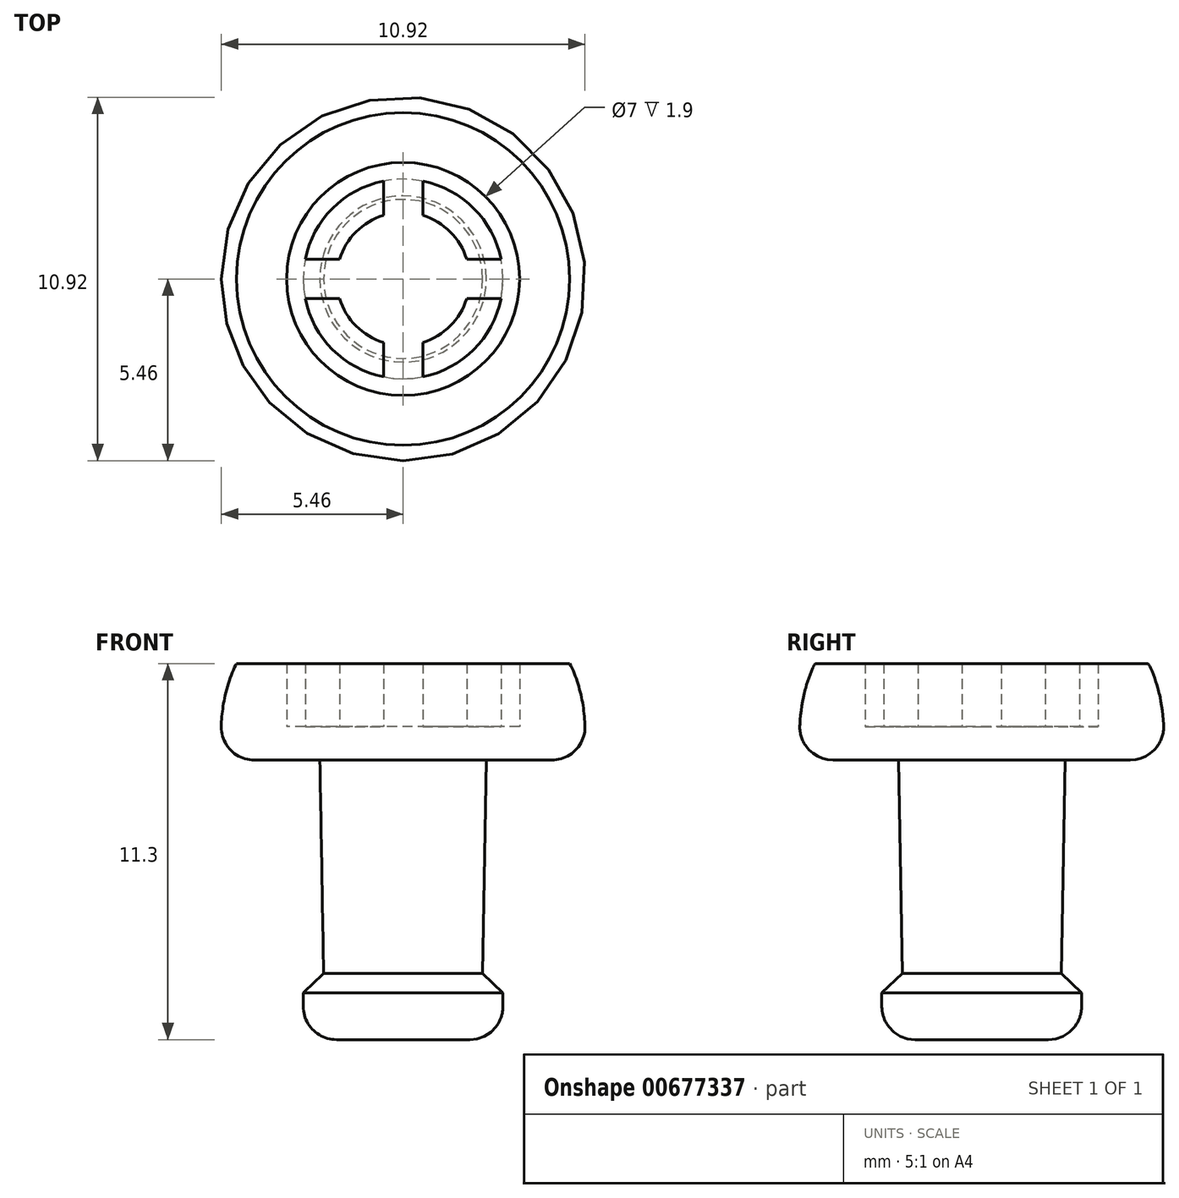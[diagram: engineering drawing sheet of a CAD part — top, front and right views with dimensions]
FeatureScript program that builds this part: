
annotation { "Feature Type Name" : "Feature", "Feature Type Description" : "" }
export const myFeature = defineFeature(function(context is Context, id is Id, definition is map)
    precondition{}
    {
        {
            var Q0;
            Q0=qCreatedBy(makeId("Top.planeOp"),FACE);
            var sketch = newSketch(context, id + "F0", { "sketchPlane" : qUnion([Q0])});
            skCircle(sketch, "E0", {"center": v(0, 0) * mm, "radius": 2 * mm});
            skCircle(sketch, "E1", {"center": v(0, 0) * mm, "radius": 3 * mm});
            skCircle(sketch, "E2", {"center": v(0, 0) * mm, "radius": 3.5 * mm});
            skCircle(sketch, "E3", {"center": v(0, 0) * mm, "radius": 5 * mm});
            skSolve(sketch);
        }
        {
            var Q0;
            Q0=makeQuery(id+"F0.imprint","IMPRINT",FACE,{"disambiguationData":[TD([[makeQuery(id+"F0.imprint","IMPRINT",EDGE,{"derivedFrom":sQuery(id+"F0.wireOp",EDGE,"E0")}),-1.0]])]});
            var Q1;
            Q1=makeQuery(id+"F0.imprint","IMPRINT",FACE,{"disambiguationData":[TD([[makeQuery(id+"F0.imprint","IMPRINT",EDGE,{"derivedFrom":sQuery(id+"F0.wireOp",EDGE,"E2")}),-1.0]])]});
            extrude(context, id + "F1", {"entities" : qUnion([Q0, Q1]), "depth" : 1.9 * mm, "offsetDistance" : 25 * mm});
        }
        {
            var Q0;
            Q0=makeQuery(id+"F1.opExtrude","CAP_FACE",FACE,{"disambiguationData":[OSD([sQuery(id+"F0.wireOp",EDGE,"E2"),sQuery(id+"F0.wireOp",EDGE,"E3")])],"isStart":true});
            var sketch = newSketch(context, id + "F2", { "sketchPlane" : qUnion([Q0])});
            skCircle(sketch, "E4", {"center": v(0, 0) * mm, "radius": 5 * mm});
            skSolve(sketch);
        }
        {
            var Q0;
            Q0 = qSketchRegion(id + "F2", true);
            extrude(context, id + "F3", {"entities" : qUnion([Q0]), "depth" : 1 * mm, "offsetDistance" : 25 * mm});
        }
        {
            var Q0;
            Q0=makeQuery(id+"F1.opExtrude","SWEPT_BODY",BODY,{"disambiguationData":[OSD([sQuery(id+"F0.wireOp",EDGE,"E0"),sQuery(id+"F0.wireOp",EDGE,"E1")])]});
            var Q1;
            Q1=makeQuery(id+"F1.opExtrude","SWEPT_BODY",BODY,{"disambiguationData":[OSD([sQuery(id+"F0.wireOp",EDGE,"E2"),sQuery(id+"F0.wireOp",EDGE,"E3")])]});
            var Q2;
            Q2=makeQuery(id+"F3.opExtrude","SWEPT_BODY",BODY,{"disambiguationData":[OSD([sQuery(id+"F2.wireOp",EDGE,"E4")])]});
            booleanBodies(context, id + "F4", {"operationType" : BooleanOperationType.UNION, "tools" : qUnion([Q0, Q1, Q2])});
        }
        {
            var Q0;
            Q0=makeQuery(id+"F1.opExtrude","CAP_FACE",FACE,{"disambiguationData":[OSD([sQuery(id+"F0.wireOp",EDGE,"E0"),sQuery(id+"F0.wireOp",EDGE,"E1")])],"isStart":false});
            var sketch = newSketch(context, id + "F5", { "sketchPlane" : qUnion([Q0])});
            skLineSegment(sketch, "E5.bottom", {"start": v(-0.6, 3.44) * mm, "end": v(0.6, 3.44) * mm});
            skLineSegment(sketch, "E5.top", {"start": v(-0.6, 0.78) * mm, "end": v(0.6, 0.78) * mm});
            skLineSegment(sketch, "E5.left", {"start": v(-0.6, 3.44) * mm, "end": v(-0.6, 0.78) * mm});
            skLineSegment(sketch, "E5.right", {"start": v(0.6, 3.44) * mm, "end": v(0.6, 0.78) * mm});
            skLineSegment(sketch, "E6.1.0", {"start": v(3.44, 0.6) * mm, "end": v(3.44, -0.6) * mm});
            skLineSegment(sketch, "E6.1.1", {"start": v(3.44, -0.6) * mm, "end": v(0.78, -0.6) * mm});
            skLineSegment(sketch, "E6.1.2", {"start": v(0.78, 0.6) * mm, "end": v(0.78, -0.6) * mm});
            skLineSegment(sketch, "E6.1.3", {"start": v(3.44, 0.6) * mm, "end": v(0.78, 0.6) * mm});
            skLineSegment(sketch, "E6.2.0", {"start": v(0.6, -3.44) * mm, "end": v(-0.6, -3.44) * mm});
            skLineSegment(sketch, "E6.2.1", {"start": v(-0.6, -3.44) * mm, "end": v(-0.6, -0.78) * mm});
            skLineSegment(sketch, "E6.2.2", {"start": v(0.6, -0.78) * mm, "end": v(-0.6, -0.78) * mm});
            skLineSegment(sketch, "E6.2.3", {"start": v(0.6, -3.44) * mm, "end": v(0.6, -0.78) * mm});
            skLineSegment(sketch, "E6.3.0", {"start": v(-3.44, -0.6) * mm, "end": v(-3.44, 0.6) * mm});
            skLineSegment(sketch, "E6.3.1", {"start": v(-3.44, 0.6) * mm, "end": v(-0.78, 0.6) * mm});
            skLineSegment(sketch, "E6.3.2", {"start": v(-0.78, -0.6) * mm, "end": v(-0.78, 0.6) * mm});
            skLineSegment(sketch, "E6.3.3", {"start": v(-3.44, -0.6) * mm, "end": v(-0.78, -0.6) * mm});
            skPoint(sketch, "E6.center", {"position": v(0, 0) * mm});
            skLineSegment(sketch, "E6.anchor1", {"start": v(0, 0) * mm, "end": v(-0.6, 0.78) * mm, "construction": true});
            skLineSegment(sketch, "E6.anchor2", {"start": v(0, 0) * mm, "end": v(-0.78, -0.6) * mm, "construction": true});
            skSolve(sketch);
        }
        {
            var Q0;
            Q0 = qSketchRegion(id + "F5", true);
            var Q1;
            Q1=makeQuery(id+"F4.opBoolean","SPLIT",FACE,{"disambiguationData":[TD([makeQuery(id+"F1.opExtrude","SWEPT_FACE",FACE,{"disambiguationData":[OSD([sQuery(id+"F0.wireOp",EDGE,"E1")])]})])],"derivedFrom":makeQuery(id+"F3.opExtrude","CAP_FACE",FACE,{"disambiguationData":[OSD([sQuery(id+"F2.wireOp",EDGE,"E4")])],"isStart":true})});
            extrude(context, id + "F6", {"entities" : qUnion([Q0]), "operationType" : NewBodyOperationType.REMOVE, "endBound" : BoundingType.UP_TO_SURFACE, "oppositeDirection" : true, "depth" : 25 * mm, "endBoundEntityFace" : qUnion([Q1]), "offsetDistance" : 25 * mm});
        }
        {
            var Q0;
            Q0=qCreatedBy(makeId("Right.planeOp"),FACE);
            var sketch = newSketch(context, id + "F7", { "sketchPlane" : qUnion([Q0])});
            skFitSpline(sketch, "E7", {"points": [v(-5, 1.9) * mm, v(-5.34, 0.95) * mm, v(-5.46, 0.05) * mm, v(-5.5, -0.77) * mm, v(-5, -1) * mm], "startDerivative": vector(-1.43, -2.3) * mm, "endDerivative": vector(7.34, -0.25) * mm});
            skLineSegment(sketch, "E8", {"start": v(-5, 1.9) * mm, "end": v(-5, -1) * mm});
            skSolve(sketch);
        }
        {
            var Q0;
            Q0=makeQuery(id+"F7.imprint","IMPRINT",FACE,{"disambiguationData":[TD([[makeQuery(id+"F7.imprint","IMPRINT",EDGE,{"derivedFrom":sQuery(id+"F7.wireOp",EDGE,"E7")}),1.0]])]});
            var Q1;
            Q1=makeQuery(id+"F3.opExtrude","CAP_EDGE",EDGE,{"disambiguationData":[OSD([sQuery(id+"F2.wireOp",EDGE,"E4")])],"isStart":false});
            revolve(context, id + "F8", {"operationType" : NewBodyOperationType.ADD, "entities" : qUnion([Q0]), "axis" : qUnion([Q1]), "revolveType" : RevolveType.FULL});
        }
        {
            var Q0;
            Q0=makeQuery(id+"F3.opExtrude","CAP_FACE",FACE,{"disambiguationData":[OSD([sQuery(id+"F2.wireOp",EDGE,"E4")])],"isStart":false});
            var sketch = newSketch(context, id + "F9", { "sketchPlane" : qUnion([Q0])});
            skCircle(sketch, "E9", {"center": v(0, 0) * mm, "radius": 2.5 * mm});
            skSolve(sketch);
        }
        {
            var Q0;
            Q0 = qSketchRegion(id + "F9", true);
            extrude(context, id + "F10", {"entities" : qUnion([Q0]), "operationType" : NewBodyOperationType.ADD, "depth" : 7 * mm, "offsetDistance" : 25 * mm, "hasDraft" : true, "draftAngle" : 1 * degree, "draftPullDirection" : true});
        }
        {
            var Q0;
            Q0=makeQuery(id+"F10.opExtrude","CAP_FACE",FACE,{"disambiguationData":[OSD([sQuery(id+"F9.wireOp",EDGE,"E9")])],"isStart":false});
            var sketch = newSketch(context, id + "F11", { "sketchPlane" : qUnion([Q0])});
            skCircle(sketch, "E10", {"center": v(0, 0) * mm, "radius": 3 * mm});
            skSolve(sketch);
        }
        {
            var Q0;
            Q0 = qSketchRegion(id + "F11", true);
            extrude(context, id + "F12", {"entities" : qUnion([Q0]), "operationType" : NewBodyOperationType.ADD, "depth" : 1.4 * mm, "offsetDistance" : 25 * mm});
        }
        {
            var Q0;
            Q0=qCreatedBy(makeId("Front.planeOp"),FACE);
            var sketch = newSketch(context, id + "F13", { "sketchPlane" : qUnion([Q0])});
            skLineSegment(sketch, "E11", {"start": v(2.36, -7.38) * mm, "end": v(3, -8) * mm});
            skLineSegment(sketch, "E12", {"start": v(3, -8) * mm, "end": v(2.38, -8) * mm});
            skLineSegment(sketch, "E13", {"start": v(2.38, -8) * mm, "end": v(2.36, -7.38) * mm});
            skSolve(sketch);
        }
        {
            var Q0;
            Q0=makeQuery(id+"F13.imprint","IMPRINT",FACE,{"disambiguationData":[TD([[makeQuery(id+"F13.imprint","IMPRINT",EDGE,{"derivedFrom":sQuery(id+"F13.wireOp",EDGE,"E11")}),-1.0]])]});
            var Q1;
            Q1=makeQuery(id+"F12.opExtrude","CAP_EDGE",EDGE,{"disambiguationData":[OSD([sQuery(id+"F11.wireOp",EDGE,"E10")])],"isStart":true});
            revolve(context, id + "F14", {"operationType" : NewBodyOperationType.ADD, "entities" : qUnion([Q0]), "axis" : qUnion([Q1]), "revolveType" : RevolveType.FULL});
        }
        {
            var Q0;
            Q0=makeQuery(id+"F12.opExtrude","CAP_EDGE",EDGE,{"disambiguationData":[OSD([sQuery(id+"F11.wireOp",EDGE,"E10")])],"isStart":false});
            var Q1;
            {var subQ0=sQuery(id+"F7.wireOp",EDGE,"E8");var subQ1=sQuery(id+"F7.wireOp",EDGE,"E7");Q1=makeQuery(id+"F8.boolean.opBoolean","MERGE",EDGE,{"derivedFrom":[makeQuery(id+"F3.opExtrude","CAP_EDGE",EDGE,{"disambiguationData":[OSD([sQuery(id+"F2.wireOp",EDGE,"E4")])],"isStart":false}),makeQuery(id+"F8.opRevolve","SWEPT_EDGE",EDGE,{"disambiguationData":[OSD([subQ1,subQ0]),TDD([makeQuery(id+"F7.imprint","INTERSECT",VERTEX,{"disambiguationData":[OD(1.0)],"derivedFrom":[subQ1,subQ0]})])]})]});}
            fillet(context, id + "F15", {"entities" : qUnion([Q0, Q1]), "radius" : 1 * mm, "tangentPropagation" : true, "allowEdgeOverflow" : false});
        }
    });
